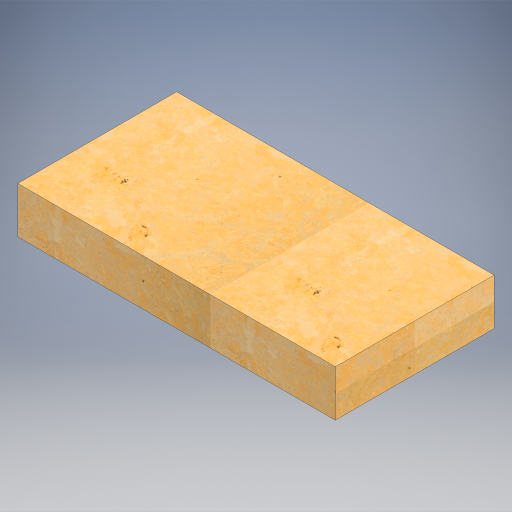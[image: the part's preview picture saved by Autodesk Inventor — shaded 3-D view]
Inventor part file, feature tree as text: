
AUTODESK INVENTOR PART (.ipt)
format: ipt  version: 2023 (Build 270158030, 158C)  size: 428,032 bytes
history: native  units: in
note: dims shown in document units (in); Inventor stores cm internally (conversion verified against a paired STEP export)
features: extrude x1, sketch x1
ambient origin geometry x8: Origin, YZ Plane, XZ Plane, XY Plane, X Axis, Y Axis, Z Axis, Center Point
bodies: Solid1 (feature_tree)
feature tree (2):
  extrude  "Extrusion1"  Depth=24.0in
  sketch  "Sketch1"  dims[d0=7.0in d1=24.0in d2=48.0in d3=0.0in]
